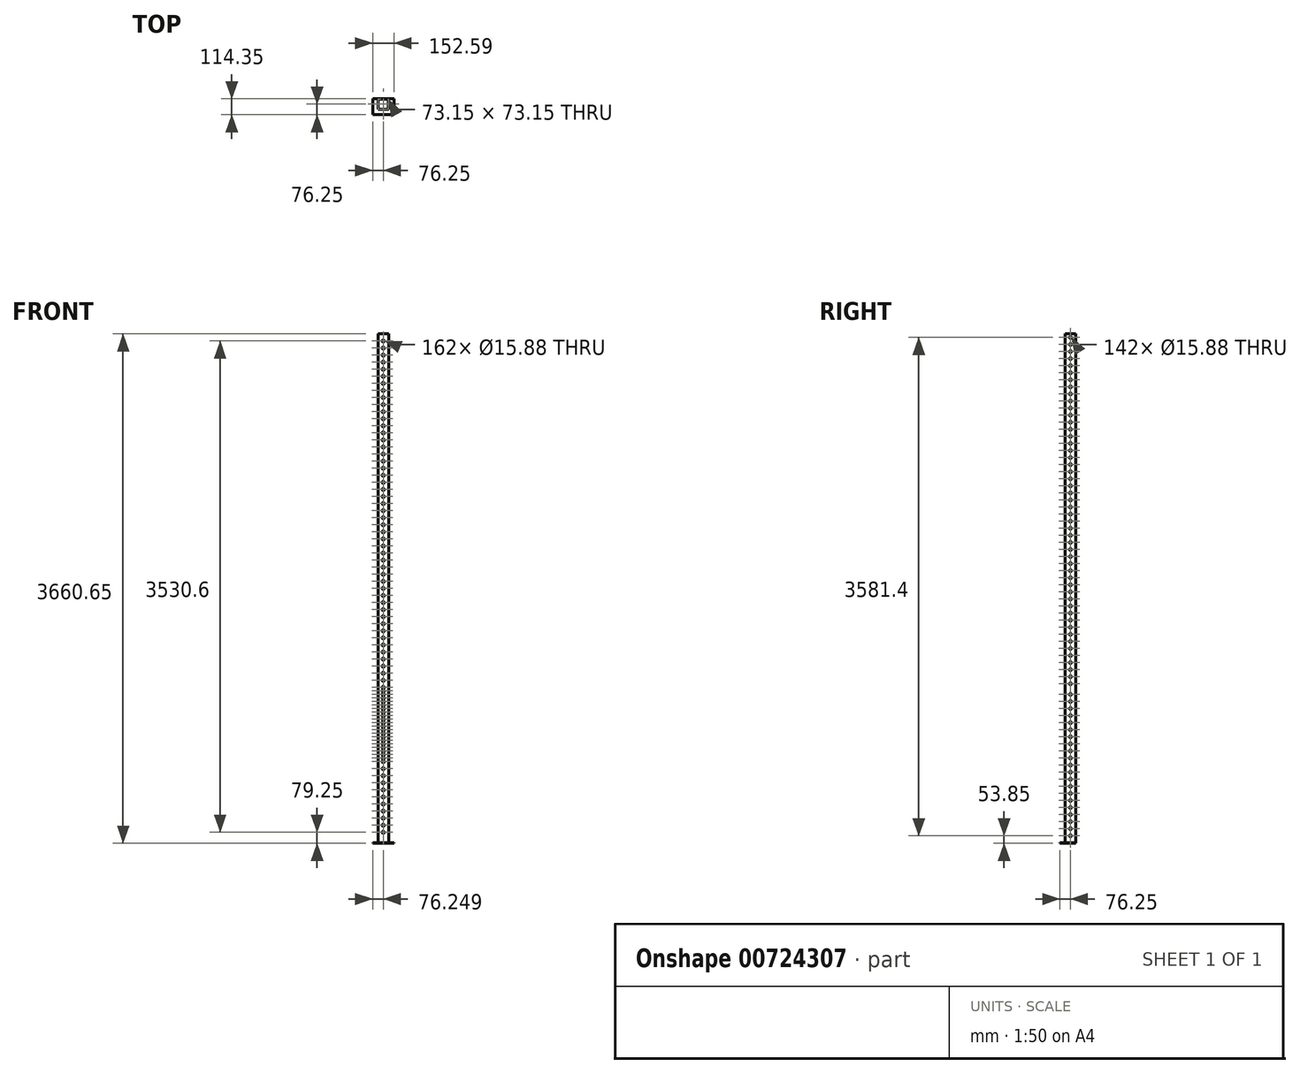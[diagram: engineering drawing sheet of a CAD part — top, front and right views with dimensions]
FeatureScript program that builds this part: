
annotation { "Feature Type Name" : "Feature", "Feature Type Description" : "" }
export const myFeature = defineFeature(function(context is Context, id is Id, definition is map)
    precondition{}
    {
        {
            var Q0;
            Q0=qCreatedBy(makeId("Top.planeOp"),FACE);
            var sketch = newSketch(context, id + "F0", { "sketchPlane" : qUnion([Q0])});
            skLineSegment(sketch, "E0.bottom", {"start": v(-38.1, -38.1) * mm, "end": v(38.1, -38.1) * mm});
            skLineSegment(sketch, "E0.top", {"start": v(-38.1, 38.1) * mm, "end": v(38.1, 38.1) * mm});
            skLineSegment(sketch, "E0.left", {"start": v(-38.1, -38.1) * mm, "end": v(-38.1, 38.1) * mm});
            skLineSegment(sketch, "E0.right", {"start": v(38.1, -38.1) * mm, "end": v(38.1, 38.1) * mm});
            skPoint(sketch, "E0.middle", {"position": v(0, 0) * mm});
            skLineSegment(sketch, "E1.bottom", {"start": v(-36.58, -36.58) * mm, "end": v(36.58, -36.58) * mm});
            skLineSegment(sketch, "E1.top", {"start": v(-36.58, 36.58) * mm, "end": v(36.58, 36.58) * mm});
            skLineSegment(sketch, "E1.left", {"start": v(-36.58, -36.58) * mm, "end": v(-36.58, 36.58) * mm});
            skLineSegment(sketch, "E1.right", {"start": v(36.58, -36.58) * mm, "end": v(36.58, 36.58) * mm});
            skLineSegment(sketch, "E2.bottom", {"start": v(-76.25, -76.25) * mm, "end": v(76.34, -76.25) * mm});
            skLineSegment(sketch, "E2.top", {"start": v(-76.25, 38.1) * mm, "end": v(76.34, 38.1) * mm});
            skLineSegment(sketch, "E2.left", {"start": v(-76.25, -76.25) * mm, "end": v(-76.25, 38.1) * mm});
            skLineSegment(sketch, "E2.right", {"start": v(76.34, -76.25) * mm, "end": v(76.34, 38.1) * mm});
            skSolve(sketch);
        }
        {
            var Q0;
            Q0=makeQuery(id+"F0.imprint","IMPRINT",FACE,{"disambiguationData":[TD([[makeQuery(id+"F0.imprint","IMPRINT",EDGE,{"derivedFrom":sQuery(id+"F0.wireOp",EDGE,"E0.bottom")}),-1.0]])]});
            extrude(context, id + "F1", {"entities" : qUnion([Q0]), "oppositeDirection" : true, "depth" : 3.05 * mm, "offsetDistance" : 25.4 * mm});
        }
        {
            var Q0;
            Q0=makeQuery(id+"F0.imprint","IMPRINT",FACE,{"disambiguationData":[TD([[makeQuery(id+"F0.imprint","IMPRINT",EDGE,{"derivedFrom":sQuery(id+"F0.wireOp",EDGE,"E0.bottom")}),1.0]])]});
            extrude(context, id + "F2", {"entities" : qUnion([Q0]), "operationType" : NewBodyOperationType.ADD, "depth" : 3657.6 * mm, "offsetDistance" : 25.4 * mm});
        }
        {
            var Q0;
            Q0=qCreatedBy(makeId("Front.planeOp"),FACE);
            cPlane(context, id + "F3", {"entities" : qUnion([Q0]), "cplaneType" : CPlaneType.OFFSET, "offset" : 76.2 * mm, "width" : 152.4 * mm, "height" : 152.4 * mm});
        }
        {
            var Q0;
            Q0=qCreatedBy(makeId("Right.planeOp"),FACE);
            cPlane(context, id + "F4", {"entities" : qUnion([Q0]), "cplaneType" : CPlaneType.OFFSET, "offset" : 76.2 * mm, "width" : 152.4 * mm, "height" : 152.4 * mm});
        }
        {
            var Q0;
            Q0=qCreatedBy(id+"F4.planeOp",FACE);
            var sketch = newSketch(context, id + "F5", { "sketchPlane" : qUnion([Q0])});
            skLineSegment(sketch, "E3.bottom", {"start": v(-38.1, 3657.6) * mm, "end": v(38.1, 3657.6) * mm});
            skLineSegment(sketch, "E3.top", {"start": v(-38.1, 0) * mm, "end": v(38.1, 0) * mm});
            skLineSegment(sketch, "E3.left", {"start": v(-38.1, 3657.6) * mm, "end": v(-38.1, 0) * mm});
            skLineSegment(sketch, "E3.right", {"start": v(38.1, 3657.6) * mm, "end": v(38.1, 0) * mm});
            skPoint(sketch, "E4", {"position": v(0, 50.8) * mm});
            skPoint(sketch, "E5.1.0.0", {"position": v(0, 101.6) * mm});
            skPoint(sketch, "E5.2.0.0", {"position": v(0, 152.4) * mm});
            skPoint(sketch, "E5.3.0.0", {"position": v(0, 203.2) * mm});
            skPoint(sketch, "E5.4.0.0", {"position": v(0, 254) * mm});
            skPoint(sketch, "E5.5.0.0", {"position": v(0, 304.8) * mm});
            skPoint(sketch, "E5.6.0.0", {"position": v(0, 355.6) * mm});
            skPoint(sketch, "E5.7.0.0", {"position": v(0, 406.4) * mm});
            skPoint(sketch, "E5.8.0.0", {"position": v(0, 457.2) * mm});
            skPoint(sketch, "E5.9.0.0", {"position": v(0, 508) * mm});
            skPoint(sketch, "E5.10.0.0", {"position": v(0, 558.8) * mm});
            skPoint(sketch, "E5.11.0.0", {"position": v(0, 609.6) * mm});
            skPoint(sketch, "E5.12.0.0", {"position": v(0, 660.4) * mm});
            skPoint(sketch, "E5.13.0.0", {"position": v(0, 711.2) * mm});
            skPoint(sketch, "E5.14.0.0", {"position": v(0, 762) * mm});
            skPoint(sketch, "E5.15.0.0", {"position": v(0, 812.8) * mm});
            skPoint(sketch, "E5.16.0.0", {"position": v(0, 863.6) * mm});
            skPoint(sketch, "E5.17.0.0", {"position": v(0, 914.4) * mm});
            skPoint(sketch, "E5.18.0.0", {"position": v(0, 965.2) * mm});
            skPoint(sketch, "E5.19.0.0", {"position": v(0, 1016) * mm});
            skPoint(sketch, "E5.20.0.0", {"position": v(0, 1066.8) * mm});
            skLineSegment(sketch, "E5.direction1", {"start": v(0, 50.8) * mm, "end": v(0, 101.6) * mm, "construction": true});
            skPoint(sketch, "E6", {"position": v(0, 1143) * mm});
            skPoint(sketch, "E7.1.0.0", {"position": v(0, 1193.8) * mm});
            skPoint(sketch, "E7.2.0.0", {"position": v(0, 1244.6) * mm});
            skPoint(sketch, "E7.3.0.0", {"position": v(0, 1295.4) * mm});
            skPoint(sketch, "E7.4.0.0", {"position": v(0, 1346.2) * mm});
            skPoint(sketch, "E7.5.0.0", {"position": v(0, 1397) * mm});
            skPoint(sketch, "E7.6.0.0", {"position": v(0, 1447.8) * mm});
            skPoint(sketch, "E7.7.0.0", {"position": v(0, 1498.6) * mm});
            skPoint(sketch, "E7.8.0.0", {"position": v(0, 1549.4) * mm});
            skPoint(sketch, "E7.9.0.0", {"position": v(0, 1600.2) * mm});
            skPoint(sketch, "E7.10.0.0", {"position": v(0, 1651) * mm});
            skPoint(sketch, "E7.11.0.0", {"position": v(0, 1701.8) * mm});
            skPoint(sketch, "E7.12.0.0", {"position": v(0, 1752.6) * mm});
            skPoint(sketch, "E7.13.0.0", {"position": v(0, 1803.4) * mm});
            skPoint(sketch, "E7.14.0.0", {"position": v(0, 1854.2) * mm});
            skPoint(sketch, "E7.15.0.0", {"position": v(0, 1905) * mm});
            skPoint(sketch, "E7.16.0.0", {"position": v(0, 1955.8) * mm});
            skPoint(sketch, "E7.17.0.0", {"position": v(0, 2006.6) * mm});
            skPoint(sketch, "E7.18.0.0", {"position": v(0, 2057.4) * mm});
            skPoint(sketch, "E7.19.0.0", {"position": v(0, 2108.2) * mm});
            skPoint(sketch, "E7.20.0.0", {"position": v(0, 2159) * mm});
            skPoint(sketch, "E7.21.0.0", {"position": v(0, 2209.8) * mm});
            skPoint(sketch, "E7.22.0.0", {"position": v(0, 2260.6) * mm});
            skPoint(sketch, "E7.23.0.0", {"position": v(0, 2311.4) * mm});
            skPoint(sketch, "E7.24.0.0", {"position": v(0, 2362.2) * mm});
            skPoint(sketch, "E7.25.0.0", {"position": v(0, 2413) * mm});
            skPoint(sketch, "E7.26.0.0", {"position": v(0, 2463.8) * mm});
            skPoint(sketch, "E7.27.0.0", {"position": v(0, 2514.6) * mm});
            skPoint(sketch, "E7.28.0.0", {"position": v(0, 2565.4) * mm});
            skPoint(sketch, "E7.29.0.0", {"position": v(0, 2616.2) * mm});
            skLineSegment(sketch, "E7.direction1", {"start": v(0, 1143) * mm, "end": v(0, 1193.8) * mm, "construction": true});
            skPoint(sketch, "E8.0.30.0", {"position": v(0, 2667) * mm});
            skPoint(sketch, "E8.0.31.0", {"position": v(0, 2717.8) * mm});
            skPoint(sketch, "E9.0.32.0", {"position": v(0, 2768.6) * mm});
            skPoint(sketch, "E9.0.33.0", {"position": v(0, 2819.4) * mm});
            skPoint(sketch, "E9.0.34.0", {"position": v(0, 2870.2) * mm});
            skPoint(sketch, "E9.0.35.0", {"position": v(0, 2921) * mm});
            skPoint(sketch, "E9.0.36.0", {"position": v(0, 2971.8) * mm});
            skPoint(sketch, "E9.0.37.0", {"position": v(0, 3022.6) * mm});
            skPoint(sketch, "E9.0.38.0", {"position": v(0, 3073.4) * mm});
            skPoint(sketch, "E9.0.39.0", {"position": v(0, 3124.2) * mm});
            skPoint(sketch, "E9.0.40.0", {"position": v(0, 3175) * mm});
            skPoint(sketch, "E9.0.41.0", {"position": v(0, 3225.8) * mm});
            skPoint(sketch, "E9.0.42.0", {"position": v(0, 3276.6) * mm});
            skPoint(sketch, "E9.0.43.0", {"position": v(0, 3327.4) * mm});
            skPoint(sketch, "E9.0.44.0", {"position": v(0, 3378.2) * mm});
            skPoint(sketch, "E9.0.45.0", {"position": v(0, 3429) * mm});
            skPoint(sketch, "E9.0.46.0", {"position": v(0, 3479.8) * mm});
            skPoint(sketch, "E9.0.47.0", {"position": v(0, 3530.6) * mm});
            skPoint(sketch, "E9.0.48.0", {"position": v(0, 3581.4) * mm});
            skPoint(sketch, "E9.0.49.0", {"position": v(0, 3632.2) * mm});
            skSolve(sketch);
        }
        {
            var Q0;
            Q0=qCreatedBy(id+"F3.planeOp",FACE);
            var sketch = newSketch(context, id + "F6", { "sketchPlane" : qUnion([Q0])});
            skLineSegment(sketch, "E10.bottom", {"start": v(-38.1, 3657.6) * mm, "end": v(38.1, 3657.6) * mm});
            skLineSegment(sketch, "E10.top", {"start": v(-38.1, 0) * mm, "end": v(38.1, 0) * mm});
            skLineSegment(sketch, "E10.left", {"start": v(-38.1, 3657.6) * mm, "end": v(-38.1, 0) * mm});
            skLineSegment(sketch, "E10.right", {"start": v(38.1, 3657.6) * mm, "end": v(38.1, 0) * mm});
            skPoint(sketch, "E11", {"position": v(0, 76.2) * mm});
            skPoint(sketch, "E12.1.0.0", {"position": v(0, 127) * mm});
            skPoint(sketch, "E12.2.0.0", {"position": v(0, 177.8) * mm});
            skPoint(sketch, "E12.3.0.0", {"position": v(0, 228.6) * mm});
            skPoint(sketch, "E12.4.0.0", {"position": v(0, 279.4) * mm});
            skPoint(sketch, "E12.5.0.0", {"position": v(0, 330.2) * mm});
            skPoint(sketch, "E12.6.0.0", {"position": v(0, 381) * mm});
            skPoint(sketch, "E12.7.0.0", {"position": v(0, 431.8) * mm});
            skPoint(sketch, "E12.8.0.0", {"position": v(0, 482.6) * mm});
            skPoint(sketch, "E12.9.0.0", {"position": v(0, 533.4) * mm});
            skLineSegment(sketch, "E12.direction1", {"start": v(0, 76.2) * mm, "end": v(0, 127) * mm, "construction": true});
            skPoint(sketch, "E13", {"position": v(0, 1168.4) * mm});
            skPoint(sketch, "E14.1.0.0", {"position": v(0, 1219.2) * mm});
            skPoint(sketch, "E14.2.0.0", {"position": v(0, 1270) * mm});
            skPoint(sketch, "E14.3.0.0", {"position": v(0, 1320.8) * mm});
            skPoint(sketch, "E14.4.0.0", {"position": v(0, 1371.6) * mm});
            skPoint(sketch, "E14.5.0.0", {"position": v(0, 1422.4) * mm});
            skPoint(sketch, "E14.6.0.0", {"position": v(0, 1473.2) * mm});
            skPoint(sketch, "E14.7.0.0", {"position": v(0, 1524) * mm});
            skPoint(sketch, "E14.8.0.0", {"position": v(0, 1574.8) * mm});
            skPoint(sketch, "E14.9.0.0", {"position": v(0, 1625.6) * mm});
            skPoint(sketch, "E14.10.0.0", {"position": v(0, 1676.4) * mm});
            skPoint(sketch, "E14.11.0.0", {"position": v(0, 1727.2) * mm});
            skPoint(sketch, "E14.12.0.0", {"position": v(0, 1778) * mm});
            skPoint(sketch, "E14.13.0.0", {"position": v(0, 1828.8) * mm});
            skPoint(sketch, "E14.14.0.0", {"position": v(0, 1879.6) * mm});
            skPoint(sketch, "E14.15.0.0", {"position": v(0, 1930.4) * mm});
            skPoint(sketch, "E14.16.0.0", {"position": v(0, 1981.2) * mm});
            skPoint(sketch, "E14.17.0.0", {"position": v(0, 2032) * mm});
            skPoint(sketch, "E14.18.0.0", {"position": v(0, 2082.8) * mm});
            skPoint(sketch, "E14.19.0.0", {"position": v(0, 2133.6) * mm});
            skPoint(sketch, "E14.20.0.0", {"position": v(0, 2184.4) * mm});
            skPoint(sketch, "E14.21.0.0", {"position": v(0, 2235.2) * mm});
            skPoint(sketch, "E14.22.0.0", {"position": v(0, 2286) * mm});
            skPoint(sketch, "E14.23.0.0", {"position": v(0, 2336.8) * mm});
            skPoint(sketch, "E14.24.0.0", {"position": v(0, 2387.6) * mm});
            skPoint(sketch, "E14.25.0.0", {"position": v(0, 2438.4) * mm});
            skPoint(sketch, "E14.26.0.0", {"position": v(0, 2489.2) * mm});
            skPoint(sketch, "E14.27.0.0", {"position": v(0, 2540) * mm});
            skPoint(sketch, "E14.28.0.0", {"position": v(0, 2590.8) * mm});
            skPoint(sketch, "E14.29.0.0", {"position": v(0, 2641.6) * mm});
            skLineSegment(sketch, "E14.direction1", {"start": v(0, 1168.4) * mm, "end": v(0, 1219.2) * mm, "construction": true});
            skPoint(sketch, "E15.0.30.0", {"position": v(0, 2692.4) * mm});
            skPoint(sketch, "E16.0.10.0", {"position": v(0, 584.2) * mm});
            skPoint(sketch, "E17.1.0.0", {"position": v(0, 609.6) * mm});
            skPoint(sketch, "E17.2.0.0", {"position": v(0, 635) * mm});
            skPoint(sketch, "E17.3.0.0", {"position": v(0, 660.4) * mm});
            skPoint(sketch, "E17.4.0.0", {"position": v(0, 685.8) * mm});
            skPoint(sketch, "E17.5.0.0", {"position": v(0, 711.2) * mm});
            skPoint(sketch, "E17.6.0.0", {"position": v(0, 736.6) * mm});
            skPoint(sketch, "E17.7.0.0", {"position": v(0, 762) * mm});
            skPoint(sketch, "E17.8.0.0", {"position": v(0, 787.4) * mm});
            skPoint(sketch, "E17.9.0.0", {"position": v(0, 812.8) * mm});
            skPoint(sketch, "E17.10.0.0", {"position": v(0, 838.2) * mm});
            skPoint(sketch, "E17.11.0.0", {"position": v(0, 863.6) * mm});
            skPoint(sketch, "E17.12.0.0", {"position": v(0, 889) * mm});
            skPoint(sketch, "E17.13.0.0", {"position": v(0, 914.4) * mm});
            skPoint(sketch, "E17.14.0.0", {"position": v(0, 939.8) * mm});
            skPoint(sketch, "E17.15.0.0", {"position": v(0, 965.2) * mm});
            skPoint(sketch, "E17.16.0.0", {"position": v(0, 990.6) * mm});
            skPoint(sketch, "E17.17.0.0", {"position": v(0, 1016) * mm});
            skPoint(sketch, "E17.18.0.0", {"position": v(0, 1041.4) * mm});
            skPoint(sketch, "E17.19.0.0", {"position": v(0, 1066.8) * mm});
            skPoint(sketch, "E17.20.0.0", {"position": v(0, 1092.2) * mm});
            skLineSegment(sketch, "E17.direction1", {"start": v(0, 584.2) * mm, "end": v(0, 609.6) * mm, "construction": true});
            skPoint(sketch, "E18.0.21.0", {"position": v(0, 1117.6) * mm});
            skPoint(sketch, "E19.0.32.0", {"position": v(0, 2794) * mm});
            skPoint(sketch, "E19.0.33.0", {"position": v(0, 2844.8) * mm});
            skPoint(sketch, "E19.0.34.0", {"position": v(0, 2895.6) * mm});
            skPoint(sketch, "E19.0.35.0", {"position": v(0, 2946.4) * mm});
            skPoint(sketch, "E19.0.36.0", {"position": v(0, 2997.2) * mm});
            skPoint(sketch, "E19.0.37.0", {"position": v(0, 3048) * mm});
            skPoint(sketch, "E19.0.38.0", {"position": v(0, 3098.8) * mm});
            skPoint(sketch, "E19.0.39.0", {"position": v(0, 3149.6) * mm});
            skPoint(sketch, "E19.0.40.0", {"position": v(0, 3200.4) * mm});
            skPoint(sketch, "E19.0.41.0", {"position": v(0, 3251.2) * mm});
            skPoint(sketch, "E19.0.42.0", {"position": v(0, 3302) * mm});
            skPoint(sketch, "E19.0.43.0", {"position": v(0, 3352.8) * mm});
            skPoint(sketch, "E19.0.44.0", {"position": v(0, 3403.6) * mm});
            skPoint(sketch, "E19.0.45.0", {"position": v(0, 3454.4) * mm});
            skPoint(sketch, "E19.0.46.0", {"position": v(0, 3505.2) * mm});
            skPoint(sketch, "E19.0.47.0", {"position": v(0, 3556) * mm});
            skPoint(sketch, "E19.0.48.0", {"position": v(0, 3606.8) * mm});
            skPoint(sketch, "E20.0.30.0", {"position": v(0, 2743.2) * mm});
            skSolve(sketch);
        }
        {
            var Q0;
            Q0=sQuery(id+"F6.wireOp",VERTEX,"E11");
            var Q1;
            Q1=sQuery(id+"F6.wireOp",VERTEX,"E12.1.0.0");
            var Q2;
            Q2=sQuery(id+"F6.wireOp",VERTEX,"E12.2.0.0");
            var Q3;
            Q3=sQuery(id+"F6.wireOp",VERTEX,"E12.3.0.0");
            var Q4;
            Q4=sQuery(id+"F6.wireOp",VERTEX,"E12.4.0.0");
            var Q5;
            Q5=sQuery(id+"F6.wireOp",VERTEX,"E12.5.0.0");
            var Q6;
            Q6=sQuery(id+"F6.wireOp",VERTEX,"E12.6.0.0");
            var Q7;
            Q7=sQuery(id+"F6.wireOp",VERTEX,"E12.7.0.0");
            var Q8;
            Q8=sQuery(id+"F6.wireOp",VERTEX,"E12.8.0.0");
            var Q9;
            Q9=sQuery(id+"F6.wireOp",VERTEX,"E12.9.0.0");
            var Q10;
            Q10=sQuery(id+"F6.wireOp",VERTEX,"E16.0.10.0");
            var Q11;
            Q11=sQuery(id+"F6.wireOp",VERTEX,"E17.1.0.0");
            var Q12;
            Q12=sQuery(id+"F6.wireOp",VERTEX,"E17.2.0.0");
            var Q13;
            Q13=sQuery(id+"F6.wireOp",VERTEX,"E17.3.0.0");
            var Q14;
            Q14=sQuery(id+"F6.wireOp",VERTEX,"E17.4.0.0");
            var Q15;
            Q15=sQuery(id+"F6.wireOp",VERTEX,"E17.5.0.0");
            var Q16;
            Q16=sQuery(id+"F6.wireOp",VERTEX,"E17.6.0.0");
            var Q17;
            Q17=sQuery(id+"F6.wireOp",VERTEX,"E17.7.0.0");
            var Q18;
            Q18=sQuery(id+"F6.wireOp",VERTEX,"E17.8.0.0");
            var Q19;
            Q19=sQuery(id+"F6.wireOp",VERTEX,"E17.9.0.0");
            var Q20;
            Q20=sQuery(id+"F6.wireOp",VERTEX,"E17.10.0.0");
            var Q21;
            Q21=sQuery(id+"F6.wireOp",VERTEX,"E17.11.0.0");
            var Q22;
            Q22=sQuery(id+"F6.wireOp",VERTEX,"E17.12.0.0");
            var Q23;
            Q23=sQuery(id+"F6.wireOp",VERTEX,"E17.13.0.0");
            var Q24;
            Q24=sQuery(id+"F6.wireOp",VERTEX,"E17.14.0.0");
            var Q25;
            Q25=sQuery(id+"F6.wireOp",VERTEX,"E17.15.0.0");
            var Q26;
            Q26=sQuery(id+"F6.wireOp",VERTEX,"E17.16.0.0");
            var Q27;
            Q27=sQuery(id+"F6.wireOp",VERTEX,"E17.17.0.0");
            var Q28;
            Q28=sQuery(id+"F6.wireOp",VERTEX,"E17.18.0.0");
            var Q29;
            Q29=sQuery(id+"F6.wireOp",VERTEX,"E17.19.0.0");
            var Q30;
            Q30=sQuery(id+"F6.wireOp",VERTEX,"E17.20.0.0");
            var Q31;
            Q31=sQuery(id+"F6.wireOp",VERTEX,"E18.0.21.0");
            var Q32;
            Q32=sQuery(id+"F6.wireOp",VERTEX,"E13");
            var Q33;
            Q33=sQuery(id+"F6.wireOp",VERTEX,"E14.1.0.0");
            var Q34;
            Q34=sQuery(id+"F6.wireOp",VERTEX,"E14.2.0.0");
            var Q35;
            Q35=sQuery(id+"F6.wireOp",VERTEX,"E14.3.0.0");
            var Q36;
            Q36=sQuery(id+"F6.wireOp",VERTEX,"E14.4.0.0");
            var Q37;
            Q37=sQuery(id+"F6.wireOp",VERTEX,"E14.5.0.0");
            var Q38;
            Q38=sQuery(id+"F6.wireOp",VERTEX,"E14.6.0.0");
            var Q39;
            Q39=sQuery(id+"F6.wireOp",VERTEX,"E14.7.0.0");
            var Q40;
            Q40=sQuery(id+"F6.wireOp",VERTEX,"E14.8.0.0");
            var Q41;
            Q41=sQuery(id+"F6.wireOp",VERTEX,"E14.9.0.0");
            var Q42;
            Q42=sQuery(id+"F6.wireOp",VERTEX,"E14.10.0.0");
            var Q43;
            Q43=sQuery(id+"F6.wireOp",VERTEX,"E14.11.0.0");
            var Q44;
            Q44=sQuery(id+"F6.wireOp",VERTEX,"E14.12.0.0");
            var Q45;
            Q45=sQuery(id+"F6.wireOp",VERTEX,"E14.13.0.0");
            var Q46;
            Q46=sQuery(id+"F6.wireOp",VERTEX,"E14.14.0.0");
            var Q47;
            Q47=sQuery(id+"F6.wireOp",VERTEX,"E14.15.0.0");
            var Q48;
            Q48=sQuery(id+"F6.wireOp",VERTEX,"E14.16.0.0");
            var Q49;
            Q49=sQuery(id+"F6.wireOp",VERTEX,"E14.17.0.0");
            var Q50;
            Q50=sQuery(id+"F6.wireOp",VERTEX,"E14.18.0.0");
            var Q51;
            Q51=sQuery(id+"F6.wireOp",VERTEX,"E14.19.0.0");
            var Q52;
            Q52=sQuery(id+"F6.wireOp",VERTEX,"E14.20.0.0");
            var Q53;
            Q53=sQuery(id+"F6.wireOp",VERTEX,"E14.21.0.0");
            var Q54;
            Q54=sQuery(id+"F6.wireOp",VERTEX,"E14.22.0.0");
            var Q55;
            Q55=sQuery(id+"F6.wireOp",VERTEX,"E14.23.0.0");
            var Q56;
            Q56=sQuery(id+"F6.wireOp",VERTEX,"E14.24.0.0");
            var Q57;
            Q57=sQuery(id+"F6.wireOp",VERTEX,"E14.25.0.0");
            var Q58;
            Q58=sQuery(id+"F6.wireOp",VERTEX,"E14.26.0.0");
            var Q59;
            Q59=sQuery(id+"F6.wireOp",VERTEX,"E14.27.0.0");
            var Q60;
            Q60=sQuery(id+"F6.wireOp",VERTEX,"E14.28.0.0");
            var Q61;
            Q61=sQuery(id+"F6.wireOp",VERTEX,"E14.29.0.0");
            var Q62;
            Q62=sQuery(id+"F6.wireOp",VERTEX,"E15.0.30.0");
            var Q63;
            Q63=sQuery(id+"F6.wireOp",VERTEX,"E19.0.32.0");
            var Q64;
            Q64=sQuery(id+"F6.wireOp",VERTEX,"E19.0.33.0");
            var Q65;
            Q65=sQuery(id+"F6.wireOp",VERTEX,"E19.0.34.0");
            var Q66;
            Q66=sQuery(id+"F6.wireOp",VERTEX,"E19.0.35.0");
            var Q67;
            Q67=sQuery(id+"F6.wireOp",VERTEX,"E19.0.36.0");
            var Q68;
            Q68=sQuery(id+"F6.wireOp",VERTEX,"E19.0.37.0");
            var Q69;
            Q69=sQuery(id+"F6.wireOp",VERTEX,"E19.0.38.0");
            var Q70;
            Q70=sQuery(id+"F6.wireOp",VERTEX,"E19.0.39.0");
            var Q71;
            Q71=sQuery(id+"F6.wireOp",VERTEX,"E19.0.40.0");
            var Q72;
            Q72=sQuery(id+"F6.wireOp",VERTEX,"E19.0.41.0");
            var Q73;
            Q73=sQuery(id+"F6.wireOp",VERTEX,"E19.0.42.0");
            var Q74;
            Q74=sQuery(id+"F6.wireOp",VERTEX,"E19.0.43.0");
            var Q75;
            Q75=sQuery(id+"F6.wireOp",VERTEX,"E19.0.44.0");
            var Q76;
            Q76=sQuery(id+"F6.wireOp",VERTEX,"E19.0.45.0");
            var Q77;
            Q77=sQuery(id+"F6.wireOp",VERTEX,"E19.0.46.0");
            var Q78;
            Q78=sQuery(id+"F6.wireOp",VERTEX,"E19.0.47.0");
            var Q79;
            Q79=sQuery(id+"F6.wireOp",VERTEX,"E19.0.48.0");
            var Q80;
            Q80=sQuery(id+"F6.wireOp",VERTEX,"E20.0.30.0");
            var Q81;
            {var subQ0=sQuery(id+"F0.wireOp",EDGE,"E0.right");var subQ1=sQuery(id+"F0.wireOp",EDGE,"E0.left");var subQ2=sQuery(id+"F0.wireOp",EDGE,"E0.top");var subQ3=sQuery(id+"F0.wireOp",EDGE,"E0.bottom");Q81=makeQuery(id+"F2.boolean.opBoolean","MERGE",BODY,{"derivedFrom":[makeQuery(id+"F1.opExtrude","SWEPT_BODY",BODY,{"disambiguationData":[OSD([subQ3,subQ2,subQ1,subQ0,sQuery(id+"F0.wireOp",EDGE,"E2.bottom"),sQuery(id+"F0.wireOp",EDGE,"E2.top"),sQuery(id+"F0.wireOp",EDGE,"E2.left"),sQuery(id+"F0.wireOp",EDGE,"E2.right")])]}),makeQuery(id+"F2.opExtrude","SWEPT_BODY",BODY,{"disambiguationData":[OSD([subQ3,subQ2,subQ1,subQ0,sQuery(id+"F0.wireOp",EDGE,"E1.bottom"),sQuery(id+"F0.wireOp",EDGE,"E1.top"),sQuery(id+"F0.wireOp",EDGE,"E1.left"),sQuery(id+"F0.wireOp",EDGE,"E1.right")])]})]});}
            hole(context, id + "F7", {"style" : HoleStyle.SIMPLE, "endStyle" : HoleEndStyle.THROUGH, "holeDiameter" : 15.88 * mm, "majorDiameter" : 6.35 * mm, "isTappedThrough" : true, "tappedDepth" : 12.7 * mm, "tapClearance" : 3, "locations" : qUnion([Q0, Q1, Q2, Q3, Q4, Q5, Q6, Q7, Q8, Q9, Q10, Q11, Q12, Q13, Q14, Q15, Q16, Q17, Q18, Q19, Q20, Q21, Q22, Q23, Q24, Q25, Q26, Q27, Q28, Q29, Q30, Q31, Q32, Q33, Q34, Q35, Q36, Q37, Q38, Q39, Q40, Q41, Q42, Q43, Q44, Q45, Q46, Q47, Q48, Q49, Q50, Q51, Q52, Q53, Q54, Q55, Q56, Q57, Q58, Q59, Q60, Q61, Q62, Q63, Q64, Q65, Q66, Q67, Q68, Q69, Q70, Q71, Q72, Q73, Q74, Q75, Q76, Q77, Q78, Q79, Q80]), "scope" : qUnion([Q81])});
        }
        {
            var Q0;
            Q0=sQuery(id+"F5.wireOp",VERTEX,"E4");
            var Q1;
            Q1=sQuery(id+"F5.wireOp",VERTEX,"E5.1.0.0");
            var Q2;
            Q2=sQuery(id+"F5.wireOp",VERTEX,"E5.2.0.0");
            var Q3;
            Q3=sQuery(id+"F5.wireOp",VERTEX,"E5.3.0.0");
            var Q4;
            Q4=sQuery(id+"F5.wireOp",VERTEX,"E5.4.0.0");
            var Q5;
            Q5=sQuery(id+"F5.wireOp",VERTEX,"E5.5.0.0");
            var Q6;
            Q6=sQuery(id+"F5.wireOp",VERTEX,"E5.6.0.0");
            var Q7;
            Q7=sQuery(id+"F5.wireOp",VERTEX,"E5.7.0.0");
            var Q8;
            Q8=sQuery(id+"F5.wireOp",VERTEX,"E5.8.0.0");
            var Q9;
            Q9=sQuery(id+"F5.wireOp",VERTEX,"E5.9.0.0");
            var Q10;
            Q10=sQuery(id+"F5.wireOp",VERTEX,"E5.10.0.0");
            var Q11;
            Q11=sQuery(id+"F5.wireOp",VERTEX,"E5.11.0.0");
            var Q12;
            Q12=sQuery(id+"F5.wireOp",VERTEX,"E5.12.0.0");
            var Q13;
            Q13=sQuery(id+"F5.wireOp",VERTEX,"E5.13.0.0");
            var Q14;
            Q14=sQuery(id+"F5.wireOp",VERTEX,"E5.14.0.0");
            var Q15;
            Q15=sQuery(id+"F5.wireOp",VERTEX,"E5.15.0.0");
            var Q16;
            Q16=sQuery(id+"F5.wireOp",VERTEX,"E5.16.0.0");
            var Q17;
            Q17=sQuery(id+"F5.wireOp",VERTEX,"E5.17.0.0");
            var Q18;
            Q18=sQuery(id+"F5.wireOp",VERTEX,"E5.18.0.0");
            var Q19;
            Q19=sQuery(id+"F5.wireOp",VERTEX,"E5.19.0.0");
            var Q20;
            Q20=sQuery(id+"F5.wireOp",VERTEX,"E5.20.0.0");
            var Q21;
            Q21=sQuery(id+"F5.wireOp",VERTEX,"E6");
            var Q22;
            Q22=sQuery(id+"F5.wireOp",VERTEX,"E7.1.0.0");
            var Q23;
            Q23=sQuery(id+"F5.wireOp",VERTEX,"E7.2.0.0");
            var Q24;
            Q24=sQuery(id+"F5.wireOp",VERTEX,"E7.3.0.0");
            var Q25;
            Q25=sQuery(id+"F5.wireOp",VERTEX,"E7.4.0.0");
            var Q26;
            Q26=sQuery(id+"F5.wireOp",VERTEX,"E7.5.0.0");
            var Q27;
            Q27=sQuery(id+"F5.wireOp",VERTEX,"E7.6.0.0");
            var Q28;
            Q28=sQuery(id+"F5.wireOp",VERTEX,"E7.7.0.0");
            var Q29;
            Q29=sQuery(id+"F5.wireOp",VERTEX,"E7.8.0.0");
            var Q30;
            Q30=sQuery(id+"F5.wireOp",VERTEX,"E7.9.0.0");
            var Q31;
            Q31=sQuery(id+"F5.wireOp",VERTEX,"E7.10.0.0");
            var Q32;
            Q32=sQuery(id+"F5.wireOp",VERTEX,"E7.11.0.0");
            var Q33;
            Q33=sQuery(id+"F5.wireOp",VERTEX,"E7.12.0.0");
            var Q34;
            Q34=sQuery(id+"F5.wireOp",VERTEX,"E7.13.0.0");
            var Q35;
            Q35=sQuery(id+"F5.wireOp",VERTEX,"E7.14.0.0");
            var Q36;
            Q36=sQuery(id+"F5.wireOp",VERTEX,"E7.15.0.0");
            var Q37;
            Q37=sQuery(id+"F5.wireOp",VERTEX,"E7.16.0.0");
            var Q38;
            Q38=sQuery(id+"F5.wireOp",VERTEX,"E7.17.0.0");
            var Q39;
            Q39=sQuery(id+"F5.wireOp",VERTEX,"E7.18.0.0");
            var Q40;
            Q40=sQuery(id+"F5.wireOp",VERTEX,"E7.19.0.0");
            var Q41;
            Q41=sQuery(id+"F5.wireOp",VERTEX,"E7.20.0.0");
            var Q42;
            Q42=sQuery(id+"F5.wireOp",VERTEX,"E7.21.0.0");
            var Q43;
            Q43=sQuery(id+"F5.wireOp",VERTEX,"E7.22.0.0");
            var Q44;
            Q44=sQuery(id+"F5.wireOp",VERTEX,"E7.23.0.0");
            var Q45;
            Q45=sQuery(id+"F5.wireOp",VERTEX,"E7.24.0.0");
            var Q46;
            Q46=sQuery(id+"F5.wireOp",VERTEX,"E7.25.0.0");
            var Q47;
            Q47=sQuery(id+"F5.wireOp",VERTEX,"E7.26.0.0");
            var Q48;
            Q48=sQuery(id+"F5.wireOp",VERTEX,"E7.27.0.0");
            var Q49;
            Q49=sQuery(id+"F5.wireOp",VERTEX,"E7.28.0.0");
            var Q50;
            Q50=sQuery(id+"F5.wireOp",VERTEX,"E7.29.0.0");
            var Q51;
            Q51=sQuery(id+"F5.wireOp",VERTEX,"E8.0.30.0");
            var Q52;
            Q52=sQuery(id+"F5.wireOp",VERTEX,"E8.0.31.0");
            var Q53;
            Q53=sQuery(id+"F5.wireOp",VERTEX,"E9.0.33.0");
            var Q54;
            Q54=sQuery(id+"F5.wireOp",VERTEX,"E9.0.34.0");
            var Q55;
            Q55=sQuery(id+"F5.wireOp",VERTEX,"E9.0.32.0");
            var Q56;
            Q56=sQuery(id+"F5.wireOp",VERTEX,"E9.0.35.0");
            var Q57;
            Q57=sQuery(id+"F5.wireOp",VERTEX,"E9.0.36.0");
            var Q58;
            Q58=sQuery(id+"F5.wireOp",VERTEX,"E9.0.37.0");
            var Q59;
            Q59=sQuery(id+"F5.wireOp",VERTEX,"E9.0.38.0");
            var Q60;
            Q60=sQuery(id+"F5.wireOp",VERTEX,"E9.0.39.0");
            var Q61;
            Q61=sQuery(id+"F5.wireOp",VERTEX,"E9.0.40.0");
            var Q62;
            Q62=sQuery(id+"F5.wireOp",VERTEX,"E9.0.41.0");
            var Q63;
            Q63=sQuery(id+"F5.wireOp",VERTEX,"E9.0.42.0");
            var Q64;
            Q64=sQuery(id+"F5.wireOp",VERTEX,"E9.0.43.0");
            var Q65;
            Q65=sQuery(id+"F5.wireOp",VERTEX,"E9.0.44.0");
            var Q66;
            Q66=sQuery(id+"F5.wireOp",VERTEX,"E9.0.45.0");
            var Q67;
            Q67=sQuery(id+"F5.wireOp",VERTEX,"E9.0.46.0");
            var Q68;
            Q68=sQuery(id+"F5.wireOp",VERTEX,"E9.0.47.0");
            var Q69;
            Q69=sQuery(id+"F5.wireOp",VERTEX,"E9.0.48.0");
            var Q70;
            Q70=sQuery(id+"F5.wireOp",VERTEX,"E9.0.49.0");
            var Q71;
            {var subQ0=sQuery(id+"F0.wireOp",EDGE,"E0.right");var subQ1=sQuery(id+"F0.wireOp",EDGE,"E0.left");var subQ2=sQuery(id+"F0.wireOp",EDGE,"E0.top");var subQ3=sQuery(id+"F0.wireOp",EDGE,"E0.bottom");Q71=makeQuery(id+"F2.boolean.opBoolean","MERGE",BODY,{"derivedFrom":[makeQuery(id+"F1.opExtrude","SWEPT_BODY",BODY,{"disambiguationData":[OSD([subQ3,subQ2,subQ1,subQ0,sQuery(id+"F0.wireOp",EDGE,"E2.bottom"),sQuery(id+"F0.wireOp",EDGE,"E2.top"),sQuery(id+"F0.wireOp",EDGE,"E2.left"),sQuery(id+"F0.wireOp",EDGE,"E2.right")])]}),makeQuery(id+"F2.opExtrude","SWEPT_BODY",BODY,{"disambiguationData":[OSD([subQ3,subQ2,subQ1,subQ0,sQuery(id+"F0.wireOp",EDGE,"E1.bottom"),sQuery(id+"F0.wireOp",EDGE,"E1.top"),sQuery(id+"F0.wireOp",EDGE,"E1.left"),sQuery(id+"F0.wireOp",EDGE,"E1.right")])]})]});}
            hole(context, id + "F8", {"style" : HoleStyle.SIMPLE, "endStyle" : HoleEndStyle.THROUGH, "holeDiameter" : 15.88 * mm, "majorDiameter" : 6.35 * mm, "isTappedThrough" : true, "tappedDepth" : 12.7 * mm, "tapClearance" : 3, "locations" : qUnion([Q0, Q1, Q2, Q3, Q4, Q5, Q6, Q7, Q8, Q9, Q10, Q11, Q12, Q13, Q14, Q15, Q16, Q17, Q18, Q19, Q20, Q21, Q22, Q23, Q24, Q25, Q26, Q27, Q28, Q29, Q30, Q31, Q32, Q33, Q34, Q35, Q36, Q37, Q38, Q39, Q40, Q41, Q42, Q43, Q44, Q45, Q46, Q47, Q48, Q49, Q50, Q51, Q52, Q53, Q54, Q55, Q56, Q57, Q58, Q59, Q60, Q61, Q62, Q63, Q64, Q65, Q66, Q67, Q68, Q69, Q70]), "scope" : qUnion([Q71])});
        }
    });
